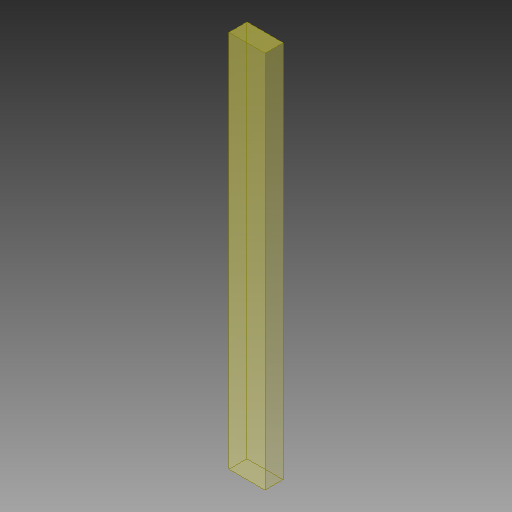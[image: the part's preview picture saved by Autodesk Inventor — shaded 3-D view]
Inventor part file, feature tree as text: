
AUTODESK INVENTOR PART (.ipt)
format: ipt  version: 2018.1 (Build 221171000, 171)  size: 91,648 bytes
history: native  units: mm
features: other x1, extrude x1, sketch x1
ambient origin geometry x8: Origin, YZ Plane, XZ Plane, XY Plane, X Axis, Y Axis, Z Axis, Center Point
bodies: Solid1 (feature_tree)
feature tree (3):
  parser-record x1  (decoder bookkeeping rows leaked as tree rows — omitted from the tree; the rows remain in map.json)
  extrude  "Extrusion1"  Depth=105.0mm
  sketch  "Sketch1"  dims[d0=10.0mm d1=105.0mm d2=5.0mm d3=0.0mm]
note: 1 file-system path scrubbed to <path> (originals preserved in map.json)
